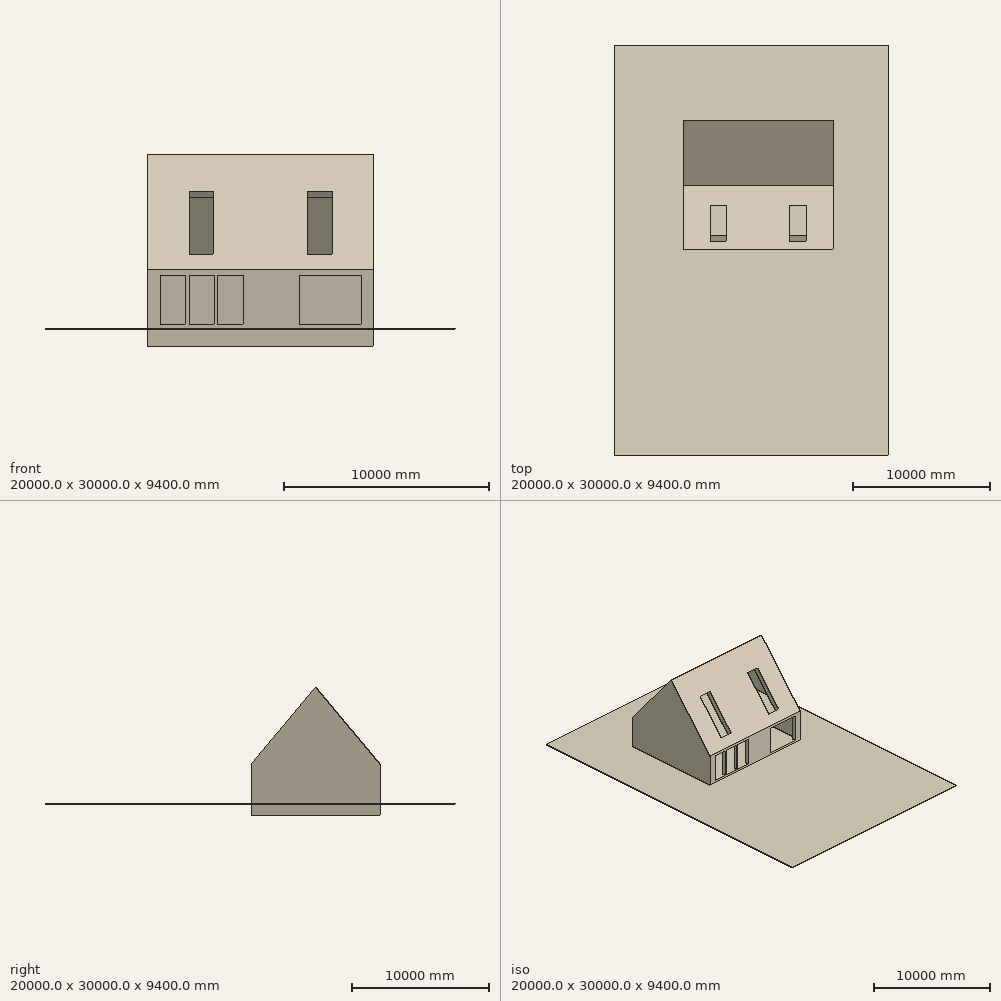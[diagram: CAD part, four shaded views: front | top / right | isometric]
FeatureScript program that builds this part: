
annotation { "Feature Type Name" : "Feature", "Feature Type Description" : "" }
export const myFeature = defineFeature(function(context is Context, id is Id, definition is map)
    precondition{}
    {
        {
            var Q0;
            Q0=qCreatedBy(makeId("Top.planeOp"),FACE);
            var sketch = newSketch(context, id + "F0", { "sketchPlane" : qUnion([Q0])});
            skLineSegment(sketch, "E0.bottom", {"start": v(0, 0) * mm, "end": v(20000, 0) * mm});
            skLineSegment(sketch, "E0.top", {"start": v(0, 30000) * mm, "end": v(20000, 30000) * mm});
            skLineSegment(sketch, "E0.left", {"start": v(0, 0) * mm, "end": v(0, 30000) * mm});
            skLineSegment(sketch, "E0.right", {"start": v(20000, 0) * mm, "end": v(20000, 30000) * mm});
            skSolve(sketch);
        }
        {
            var Q0;
            Q0=makeQuery(id+"F0.imprint","IMPRINT",FACE,{"disambiguationData":[TD([[makeQuery(id+"F0.imprint","IMPRINT",EDGE,{"derivedFrom":sQuery(id+"F0.wireOp",EDGE,"E0.bottom")}),1.0]])]});
            extrude(context, id + "F1", {"entities" : qUnion([Q0]), "oppositeDirection" : true, "depth" : 50 * mm});
        }
        {
            var Q0;
            Q0=makeQuery(id+"F1.opExtrude","CAP_FACE",FACE,{"disambiguationData":[OSD([sQuery(id+"F0.wireOp",EDGE,"E0.bottom"),sQuery(id+"F0.wireOp",EDGE,"E0.top"),sQuery(id+"F0.wireOp",EDGE,"E0.left"),sQuery(id+"F0.wireOp",EDGE,"E0.right")])],"isStart":true});
            var sketch = newSketch(context, id + "F2", { "sketchPlane" : qUnion([Q0])});
            skLineSegment(sketch, "E1.bottom", {"start": v(16000, 24500) * mm, "end": v(5000, 24500) * mm});
            skLineSegment(sketch, "E1.top", {"start": v(16000, 15050) * mm, "end": v(5000, 15050) * mm});
            skLineSegment(sketch, "E1.left", {"start": v(16000, 24500) * mm, "end": v(16000, 15050) * mm});
            skLineSegment(sketch, "E1.right", {"start": v(5000, 24500) * mm, "end": v(5000, 15050) * mm});
            skLineSegment(sketch, "E2.0", {"start": v(15600, 15450) * mm, "end": v(5400, 15450) * mm});
            skLineSegment(sketch, "E2.1", {"start": v(15600, 24100) * mm, "end": v(15600, 15450) * mm});
            skLineSegment(sketch, "E2.2", {"start": v(15600, 24100) * mm, "end": v(5400, 24100) * mm});
            skLineSegment(sketch, "E2.3", {"start": v(5400, 24100) * mm, "end": v(5400, 15450) * mm});
            skSolve(sketch);
        }
        {
            var Q0;
            Q0=makeQuery(id+"F2.imprint","IMPRINT",FACE,{"disambiguationData":[TD([[makeQuery(id+"F2.imprint","IMPRINT",EDGE,{"derivedFrom":sQuery(id+"F2.wireOp",EDGE,"E1.bottom")}),1.0]])]});
            extrude(context, id + "F3", {"entities" : qUnion([Q0]), "operationType" : NewBodyOperationType.ADD, "oppositeDirection" : true, "depth" : 900 * mm});
        }
        {
            var Q0;
            Q0=makeQuery(id+"F2.imprint","IMPRINT",FACE,{"disambiguationData":[TD([[makeQuery(id+"F2.imprint","IMPRINT",EDGE,{"derivedFrom":sQuery(id+"F2.wireOp",EDGE,"E1.bottom")}),1.0]])]});
            extrude(context, id + "F4", {"entities" : qUnion([Q0]), "operationType" : NewBodyOperationType.ADD, "depth" : 200 * mm});
        }
        {
            var Q0;
            Q0=makeQuery(id+"F4.opExtrude","CAP_FACE",FACE,{"disambiguationData":[OSD([sQuery(id+"F2.wireOp",EDGE,"E1.bottom"),sQuery(id+"F2.wireOp",EDGE,"E1.top"),sQuery(id+"F2.wireOp",EDGE,"E1.left"),sQuery(id+"F2.wireOp",EDGE,"E1.right"),sQuery(id+"F2.wireOp",EDGE,"E2.0"),sQuery(id+"F2.wireOp",EDGE,"E2.1"),sQuery(id+"F2.wireOp",EDGE,"E2.2"),sQuery(id+"F2.wireOp",EDGE,"E2.3")])],"isStart":false});
            var sketch = newSketch(context, id + "F5", { "sketchPlane" : qUnion([Q0])});
            skLineSegment(sketch, "E3.bottom", {"start": v(5400, 15450) * mm, "end": v(15600, 15450) * mm});
            skLineSegment(sketch, "E3.top", {"start": v(5400, 24100) * mm, "end": v(15600, 24100) * mm});
            skLineSegment(sketch, "E3.left", {"start": v(5400, 15450) * mm, "end": v(5400, 24100) * mm});
            skLineSegment(sketch, "E3.right", {"start": v(15600, 15450) * mm, "end": v(15600, 24100) * mm});
            skSolve(sketch);
        }
        {
            var Q0;
            Q0 = qSketchRegion(id + "F5", true);
            extrude(context, id + "F6", {"entities" : qUnion([Q0]), "operationType" : NewBodyOperationType.ADD, "oppositeDirection" : true, "depth" : 20 * mm});
        }
        {
            var Q0;
            Q0=makeQuery(id+"F6.boolean.opBoolean","MERGE",FACE,{"derivedFrom":[makeQuery(id+"F4.opExtrude","CAP_FACE",FACE,{"disambiguationData":[OSD([sQuery(id+"F2.wireOp",EDGE,"E1.bottom"),sQuery(id+"F2.wireOp",EDGE,"E1.top"),sQuery(id+"F2.wireOp",EDGE,"E1.left"),sQuery(id+"F2.wireOp",EDGE,"E1.right"),sQuery(id+"F2.wireOp",EDGE,"E2.0"),sQuery(id+"F2.wireOp",EDGE,"E2.1"),sQuery(id+"F2.wireOp",EDGE,"E2.2"),sQuery(id+"F2.wireOp",EDGE,"E2.3")])],"isStart":false}),makeQuery(id+"F6.opExtrude","CAP_FACE",FACE,{"disambiguationData":[OSD([sQuery(id+"F5.wireOp",EDGE,"E3.bottom"),sQuery(id+"F5.wireOp",EDGE,"E3.top"),sQuery(id+"F5.wireOp",EDGE,"E3.left"),sQuery(id+"F5.wireOp",EDGE,"E3.right")])],"isStart":true})]});
            var sketch = newSketch(context, id + "F7", { "sketchPlane" : qUnion([Q0])});
            skLineSegment(sketch, "E4.bottom", {"start": v(5000, 15050) * mm, "end": v(16000, 15050) * mm});
            skLineSegment(sketch, "E4.top", {"start": v(5000, 24500) * mm, "end": v(16000, 24500) * mm});
            skLineSegment(sketch, "E4.left", {"start": v(5000, 15050) * mm, "end": v(5000, 24500) * mm});
            skLineSegment(sketch, "E4.right", {"start": v(16000, 15050) * mm, "end": v(16000, 24500) * mm});
            skLineSegment(sketch, "E5.0", {"start": v(5300, 15350) * mm, "end": v(5300, 24200) * mm});
            skLineSegment(sketch, "E5.1", {"start": v(5300, 15350) * mm, "end": v(15700, 15350) * mm});
            skLineSegment(sketch, "E5.2", {"start": v(15700, 15350) * mm, "end": v(15700, 24200) * mm});
            skLineSegment(sketch, "E5.3", {"start": v(5300, 24200) * mm, "end": v(15700, 24200) * mm});
            skSolve(sketch);
        }
        {
            var Q0;
            Q0 = qSketchRegion(id + "F7", true);
            extrude(context, id + "F8", {"entities" : qUnion([Q0]), "operationType" : NewBodyOperationType.ADD, "depth" : 2650 * mm});
        }
        {
            var Q0;
            Q0=makeQuery(id+"F8.boolean.opBoolean","MERGE",FACE,{"derivedFrom":[makeQuery(id+"F4.opExtrude","SWEPT_FACE",FACE,{"disambiguationData":[OSD([sQuery(id+"F2.wireOp",EDGE,"E1.left")])]}),makeQuery(id+"F8.opExtrude","SWEPT_FACE",FACE,{"disambiguationData":[OSD([sQuery(id+"F7.wireOp",EDGE,"E4.right")])]})]});
            var sketch = newSketch(context, id + "F9", { "sketchPlane" : qUnion([Q0])});
            skLineSegment(sketch, "E6", {"start": v(15050, 2850) * mm, "end": v(24500, 2850) * mm});
            skLineSegment(sketch, "E7", {"start": v(24500, 2850) * mm, "end": v(19775, 8500) * mm});
            skLineSegment(sketch, "E8", {"start": v(19775, 8500) * mm, "end": v(15050, 2850) * mm});
            skLineSegment(sketch, "E9", {"start": v(15952.68, 3150) * mm, "end": v(23597.32, 3150) * mm});
            skLineSegment(sketch, "E10", {"start": v(23597.32, 3150) * mm, "end": v(19775, 7720.6) * mm});
            skLineSegment(sketch, "E11", {"start": v(19775, 7720.6) * mm, "end": v(15952.68, 3150) * mm});
            skSolve(sketch);
        }
        {
            var Q0;
            Q0=makeQuery(id+"F9.imprint","IMPRINT",FACE,{"disambiguationData":[TD([[makeQuery(id+"F9.imprint","IMPRINT",EDGE,{"derivedFrom":sQuery(id+"F9.wireOp",EDGE,"E6")}),-1.0]])]});
            var Q1;
            Q1=makeQuery(id+"F8.boolean.opBoolean","MERGE",FACE,{"derivedFrom":[makeQuery(id+"F4.opExtrude","SWEPT_FACE",FACE,{"disambiguationData":[OSD([sQuery(id+"F2.wireOp",EDGE,"E1.right")])]}),makeQuery(id+"F8.opExtrude","SWEPT_FACE",FACE,{"disambiguationData":[OSD([sQuery(id+"F7.wireOp",EDGE,"E4.left")])]})]});
            extrude(context, id + "F10", {"entities" : qUnion([Q0]), "operationType" : NewBodyOperationType.ADD, "endBound" : BoundingType.UP_TO_SURFACE, "oppositeDirection" : true, "endBoundEntityFace" : qUnion([Q1]), "depth" : 25 * mm});
        }
        {
            var Q0;
            Q0=makeQuery(id+"F10.boolean.opBoolean","MERGE",FACE,{"derivedFrom":[makeQuery(id+"F8.boolean.opBoolean","MERGE",FACE,{"derivedFrom":[makeQuery(id+"F4.opExtrude","SWEPT_FACE",FACE,{"disambiguationData":[OSD([sQuery(id+"F2.wireOp",EDGE,"E1.left")])]}),makeQuery(id+"F8.opExtrude","SWEPT_FACE",FACE,{"disambiguationData":[OSD([sQuery(id+"F7.wireOp",EDGE,"E4.right")])]})]}),makeQuery(id+"F10.opExtrude","CAP_FACE",FACE,{"disambiguationData":[OSD([sQuery(id+"F9.wireOp",EDGE,"E6"),sQuery(id+"F9.wireOp",EDGE,"E7"),sQuery(id+"F9.wireOp",EDGE,"E8"),sQuery(id+"F9.wireOp",EDGE,"E9"),sQuery(id+"F9.wireOp",EDGE,"E10"),sQuery(id+"F9.wireOp",EDGE,"E11")])],"isStart":true})]});
            var sketch = newSketch(context, id + "F11", { "sketchPlane" : qUnion([Q0])});
            skLineSegment(sketch, "E12", {"start": v(15952.68, 3150) * mm, "end": v(19775, 7720.6) * mm});
            skLineSegment(sketch, "E13", {"start": v(19775, 7720.6) * mm, "end": v(23597.32, 3150) * mm});
            skLineSegment(sketch, "E14", {"start": v(23597.32, 3150) * mm, "end": v(15952.68, 3150) * mm});
            skSolve(sketch);
        }
        {
            var Q0;
            Q0=makeQuery(id+"F11.imprint","IMPRINT",FACE,{"disambiguationData":[TD([[makeQuery(id+"F11.imprint","IMPRINT",EDGE,{"derivedFrom":sQuery(id+"F11.wireOp",EDGE,"E12")}),1.0]])]});
            extrude(context, id + "F12", {"entities" : qUnion([Q0]), "operationType" : NewBodyOperationType.ADD, "oppositeDirection" : true, "depth" : 400 * mm});
        }
        {
            var Q0;
            {var subQ0=sQuery(id+"F7.wireOp",EDGE,"E4.left");var subQ1=sQuery(id+"F2.wireOp",EDGE,"E1.right");Q0=makeQuery(id+"F10.boolean.opBoolean","MERGE",FACE,{"derivedFrom":[makeQuery(id+"F8.boolean.opBoolean","MERGE",FACE,{"derivedFrom":[makeQuery(id+"F4.opExtrude","SWEPT_FACE",FACE,{"disambiguationData":[OSD([subQ1])]}),makeQuery(id+"F8.opExtrude","SWEPT_FACE",FACE,{"disambiguationData":[OSD([subQ0])]})]}),makeQuery(id+"F10.opExtrude","CAP_FACE",FACE,{"disambiguationData":[OSD([subQ1,subQ0])],"isStart":false})]});}
            var sketch = newSketch(context, id + "F13", { "sketchPlane" : qUnion([Q0])});
            skLineSegment(sketch, "E15", {"start": v(-23597.32, 3150) * mm, "end": v(-19775, 7720.6) * mm});
            skLineSegment(sketch, "E16", {"start": v(-19775, 7720.6) * mm, "end": v(-15952.68, 3150) * mm});
            skLineSegment(sketch, "E17", {"start": v(-15952.68, 3150) * mm, "end": v(-23597.32, 3150) * mm});
            skSolve(sketch);
        }
        {
            var Q0;
            Q0=makeQuery(id+"F13.imprint","IMPRINT",FACE,{"disambiguationData":[TD([[makeQuery(id+"F13.imprint","IMPRINT",EDGE,{"derivedFrom":sQuery(id+"F13.wireOp",EDGE,"E15")}),1.0]])]});
            extrude(context, id + "F14", {"entities" : qUnion([Q0]), "operationType" : NewBodyOperationType.ADD, "oppositeDirection" : true, "depth" : 400 * mm});
        }
        {
            var Q0;
            Q0=makeQuery(id+"F8.boolean.opBoolean","MERGE",FACE,{"derivedFrom":[makeQuery(id+"F4.opExtrude","SWEPT_FACE",FACE,{"disambiguationData":[OSD([sQuery(id+"F2.wireOp",EDGE,"E1.top")])]}),makeQuery(id+"F8.opExtrude","SWEPT_FACE",FACE,{"disambiguationData":[OSD([sQuery(id+"F7.wireOp",EDGE,"E4.bottom")])]})]});
            var sketch = newSketch(context, id + "F15", { "sketchPlane" : qUnion([Q0])});
            skSolve(sketch);
        }
        {
            var Q0;
            {var subQ0=sQuery(id+"F2.wireOp",EDGE,"E1.top");Q0=makeQuery(id+"F15.imprint","IMPRINT",FACE,{"disambiguationData":[TD([[makeQuery(id+"F15.imprint","IMPRINT",EDGE,{"derivedFrom":makeQuery(id+"F4.opExtrude","CAP_EDGE",EDGE,{"disambiguationData":[OSD([subQ0])],"isStart":true})}),-1.0]])]});}
            var sketch = newSketch(context, id + "F16", { "sketchPlane" : qUnion([Q0])});
            skLineSegment(sketch, "E18.bottom", {"start": v(5600, 2600) * mm, "end": v(6850, 2600) * mm});
            skLineSegment(sketch, "E18.top", {"start": v(5600, 200) * mm, "end": v(6850, 200) * mm});
            skLineSegment(sketch, "E18.left", {"start": v(5600, 2600) * mm, "end": v(5600, 200) * mm});
            skLineSegment(sketch, "E18.right", {"start": v(6850, 2600) * mm, "end": v(6850, 200) * mm});
            skLineSegment(sketch, "E19.bottom", {"start": v(7000, 2600) * mm, "end": v(8250, 2600) * mm});
            skLineSegment(sketch, "E19.top", {"start": v(7000, 200) * mm, "end": v(8250, 200) * mm});
            skLineSegment(sketch, "E19.left", {"start": v(7000, 2600) * mm, "end": v(7000, 200) * mm});
            skLineSegment(sketch, "E19.right", {"start": v(8250, 2600) * mm, "end": v(8250, 200) * mm});
            skLineSegment(sketch, "E20.bottom", {"start": v(12400, 2600) * mm, "end": v(15400, 2600) * mm});
            skLineSegment(sketch, "E20.top", {"start": v(12400, 200) * mm, "end": v(15400, 200) * mm});
            skLineSegment(sketch, "E20.left", {"start": v(12400, 2600) * mm, "end": v(12400, 200) * mm});
            skLineSegment(sketch, "E20.right", {"start": v(15400, 2600) * mm, "end": v(15400, 200) * mm});
            skLineSegment(sketch, "E21.bottom", {"start": v(8400, 2600) * mm, "end": v(9650, 2600) * mm});
            skLineSegment(sketch, "E21.top", {"start": v(8400, 200) * mm, "end": v(9650, 200) * mm});
            skLineSegment(sketch, "E21.left", {"start": v(8400, 2600) * mm, "end": v(8400, 200) * mm});
            skLineSegment(sketch, "E21.right", {"start": v(9650, 2600) * mm, "end": v(9650, 200) * mm});
            skSolve(sketch);
        }
        {
            var Q0;
            Q0 = qSketchRegion(id + "F16", true);
            extrude(context, id + "F17", {"entities" : qUnion([Q0]), "operationType" : NewBodyOperationType.REMOVE, "oppositeDirection" : true, "depth" : 300 * mm});
        }
        {
            var Q0;
            Q0=makeQuery(id+"F10.opExtrude","SWEPT_FACE",FACE,{"disambiguationData":[OSD([sQuery(id+"F9.wireOp",EDGE,"E8")])]});
            var sketch = newSketch(context, id + "F18", { "sketchPlane" : qUnion([Q0])});
            skLineSegment(sketch, "E22.bottom", {"start": v(7000, 16841.11) * mm, "end": v(8200, 16841.11) * mm});
            skLineSegment(sketch, "E22.top", {"start": v(7000, 12841.11) * mm, "end": v(8200, 12841.11) * mm});
            skLineSegment(sketch, "E22.left", {"start": v(7000, 16841.11) * mm, "end": v(7000, 12841.11) * mm});
            skLineSegment(sketch, "E22.right", {"start": v(8200, 16841.11) * mm, "end": v(8200, 12841.11) * mm});
            skLineSegment(sketch, "E23.bottom", {"start": v(12800, 16841.11) * mm, "end": v(14000, 16841.11) * mm});
            skLineSegment(sketch, "E23.top", {"start": v(12800, 12841.11) * mm, "end": v(14000, 12841.11) * mm});
            skLineSegment(sketch, "E23.left", {"start": v(12800, 16841.11) * mm, "end": v(12800, 12841.11) * mm});
            skLineSegment(sketch, "E23.right", {"start": v(14000, 16841.11) * mm, "end": v(14000, 12841.11) * mm});
            skSolve(sketch);
        }
        {
            var Q0;
            Q0=makeQuery(id+"F18.imprint","IMPRINT",FACE,{"disambiguationData":[TD([[makeQuery(id+"F18.imprint","IMPRINT",EDGE,{"derivedFrom":sQuery(id+"F18.wireOp",EDGE,"E22.bottom")}),-1.0]])]});
            var Q1;
            Q1=makeQuery(id+"F18.imprint","IMPRINT",FACE,{"disambiguationData":[TD([[makeQuery(id+"F18.imprint","IMPRINT",EDGE,{"derivedFrom":sQuery(id+"F18.wireOp",EDGE,"E23.bottom")}),-1.0]])]});
            extrude(context, id + "F19", {"entities" : qUnion([Q0, Q1]), "operationType" : NewBodyOperationType.REMOVE, "oppositeDirection" : true, "depth" : 500 * mm});
        }
    });
